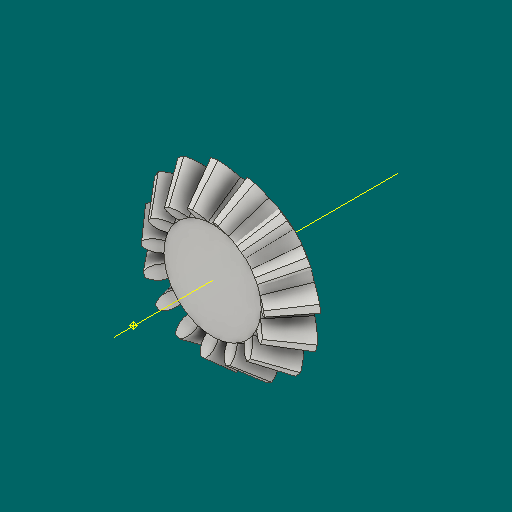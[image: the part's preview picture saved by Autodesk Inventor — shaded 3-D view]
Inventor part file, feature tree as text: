
AUTODESK INVENTOR PART (.ipt)
format: ipt  version: 2023.1 (Build 271208000, 208)  size: 481,792 bytes
history: native  units: mm
features: other x24, loft x2, pattern_circular x2, sketch x1
ambient origin geometry x6: Origin, XZ Plane, X Axis, Y Axis, Z Axis, Center Point
bodies: Solid1 (feature_tree)
feature tree (29):
  other  "Top Point"
  other  "Mesh Plane2"
  other  "Teeth Body"
  other  "Start Point"
  other  "Tooth Plane"
  other  "Start Sketch"
  other  "End Point"
  other  "3D Sketch Right"
  other  "End Plane Right"
  loft  "Loft Right"
  pattern_circular  "Circular Pattern Right"  [2 undecoded]
  other  "3D Sketch Left"
  other  "End Plane Left"
  loft  "Loft Left"
  pattern_circular  "Circular Pattern Left"  [2 undecoded]
  other  "Fix Body"
  other  "Mesh Plane"
  other  "Top Plane"
  other  "Teeth Body Sketch"
  other  "End Plane"
  other  "End Sketch"
  other  "Helical Curve Left"
  other  "End Sketch Left"
  other  "Body Sketch"
  sketch  "Sketch6"  dims[d0=19.05mm d1=16.6116mm d2=21.082mm d3=4.7625mm d4=11.938mm d5=90.0deg d7=3.541063mm d8=4.298783mm d9=10.586735mm d11=4.9022mm d12=2.447583mm d15=2.971319mm d16=7.317551mm d17=0.0mm d18=90.0deg d19=0.0mm d20=90.0deg d21=150.0mm d22=360.0deg d26=70.487871mm d27=3.92176mm d28=19.05mm d29=-6.435011mm d30=2.447583mm d31=2.971319mm d32=7.317551mm d35=0.0mm d37=0.0mm d39=0.0mm d40=90.0deg d41=150.0mm d42=360.0deg d46=90.0deg d47=90.0deg d48=0.0mm d49=0.0mm d50=90.0deg d51=2.094395mm d52=0.0mm d53=0.0mm d54=0.0mm d56=5.901499mm d57=14.01445mm d58=10.04697mm d59=9.686788mm d60=6.944466mm d61=9.686788mm d62=6.944466mm d63=90.0deg d64=90.0deg d65=70.487871mm d66=31.5mm d67=19.05mm d68=-6.435011mm d69=3.92176mm d70=2.971319mm d71=7.317551mm d72=2.447583mm d73=6.944466mm d74=9.686788mm d75=0.0mm d76=90.0deg d77=0.0mm d78=90.0deg d79=0.0mm d80=90.0deg d81=150.0mm d82=360.0deg d84=10.0mm d85=20.0mm d86=20.0mm d87=10.0mm d88=0.0mm d89=0.0mm]
  other  "Srf1"
  other  "Helical Curve Right"
  other  "End Sketch Right"
  other  "Pitch Diameter"
note: 4 required parameter values undecoded (feature->parameter linkage not recoverable at this tier; creation-order binding heuristic only, values carry confidence <= 0.55)
